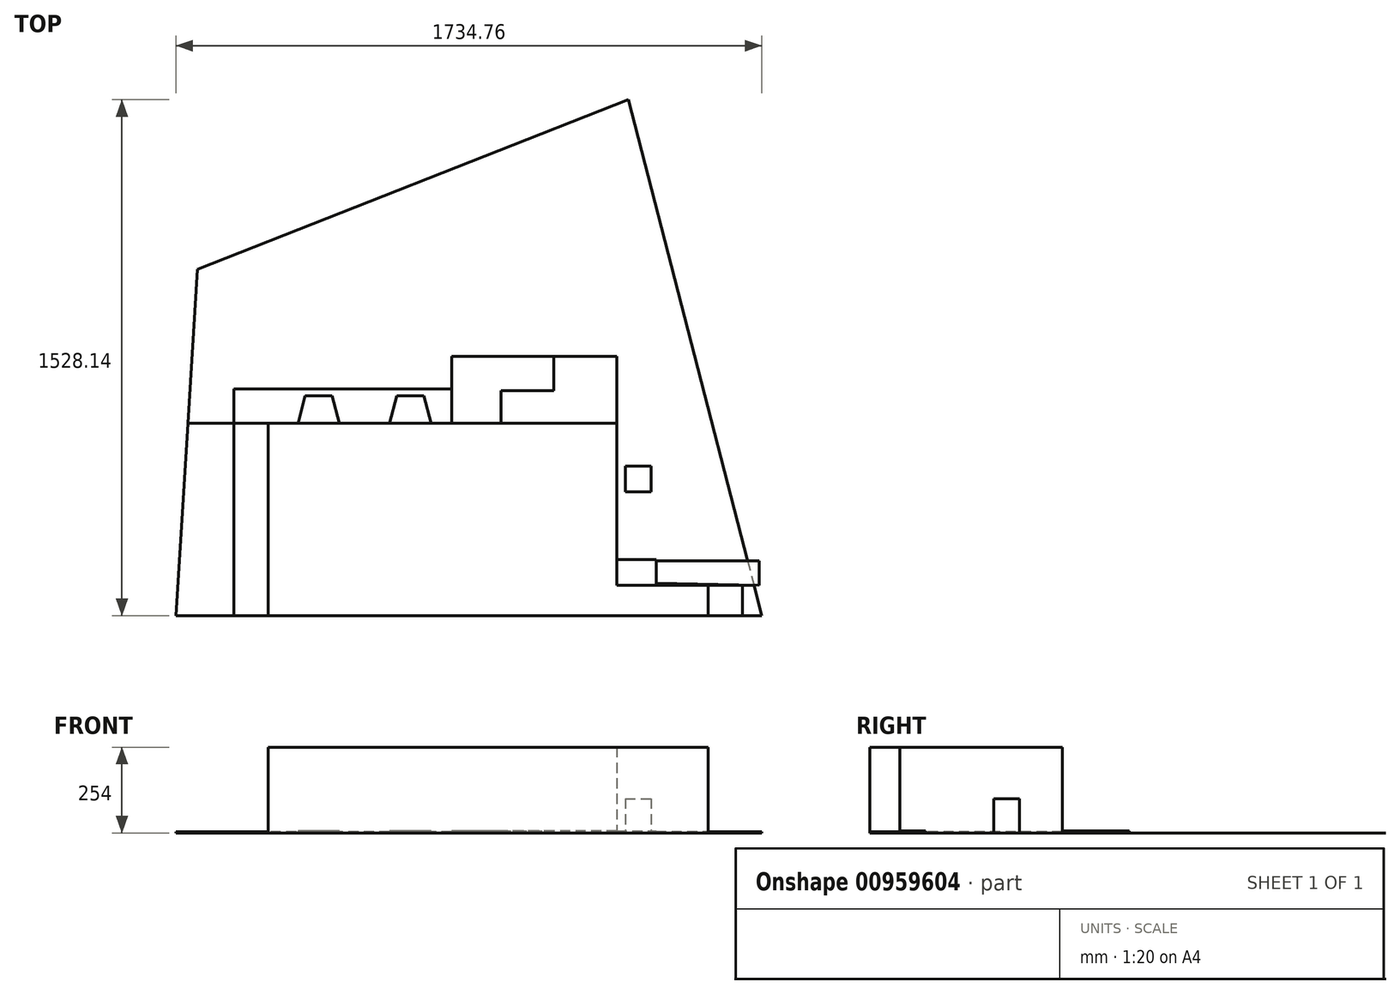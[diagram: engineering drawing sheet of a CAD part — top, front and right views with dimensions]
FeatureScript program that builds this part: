
annotation { "Feature Type Name" : "Feature", "Feature Type Description" : "" }
export const myFeature = defineFeature(function(context is Context, id is Id, definition is map)
    precondition{}
    {
        {
            var Q0;
            Q0=qCreatedBy(makeId("Top.planeOp"),FACE);
            var sketch = newSketch(context, id + "F0", { "sketchPlane" : qUnion([Q0])});
            skLineSegment(sketch, "E0", {"start": v(0, 0) * mm, "end": v(-1270, 0) * mm});
            skLineSegment(sketch, "E1", {"start": v(-1270, 0) * mm, "end": v(-1241.79, 456.33) * mm});
            skLineSegment(sketch, "E2", {"start": v(-1241.79, 456.33) * mm, "end": v(34.7, 958.18) * mm});
            skLineSegment(sketch, "E3", {"start": v(34.7, 958.18) * mm, "end": v(406.4, -480.48) * mm});
            skLineSegment(sketch, "E4", {"start": v(406.4, -480.48) * mm, "end": v(0, -480.48) * mm});
            skLineSegment(sketch, "E5", {"start": v(0, -480.48) * mm, "end": v(0, 0) * mm});
            skSolve(sketch);
        }
        {
            var Q0;
            Q0=makeQuery(id+"F0.imprint","IMPRINT",FACE,{"disambiguationData":[TD([[makeQuery(id+"F0.imprint","IMPRINT",EDGE,{"derivedFrom":sQuery(id+"F0.wireOp",EDGE,"E0")}),-1.0]])]});
            var sketch = newSketch(context, id + "F1", { "sketchPlane" : qUnion([Q0])});
            skLineSegment(sketch, "E6", {"start": v(-1032.93, 0) * mm, "end": v(0, 0) * mm});
            skLineSegment(sketch, "E7", {"start": v(0, 0) * mm, "end": v(0, -480.48) * mm});
            skLineSegment(sketch, "E8", {"start": v(0, -480.48) * mm, "end": v(270.93, -480.48) * mm});
            skLineSegment(sketch, "E9", {"start": v(270.93, -480.48) * mm, "end": v(270.93, -569.96) * mm});
            skLineSegment(sketch, "E10", {"start": v(270.93, -569.96) * mm, "end": v(-1032.93, -569.96) * mm});
            skLineSegment(sketch, "E11", {"start": v(-1032.93, -569.96) * mm, "end": v(-1032.93, 0) * mm});
            skSolve(sketch);
        }
        {
            var Q0;
            Q0 = qSketchRegion(id + "F1", true);
            extrude(context, id + "F2", {"entities" : qUnion([Q0]), "depth" : 254 * mm, "offsetDistance" : 25.4 * mm});
        }
        {
            var Q0;
            Q0=makeQuery(id+"F0.imprint","IMPRINT",FACE,{"disambiguationData":[TD([[makeQuery(id+"F0.imprint","IMPRINT",EDGE,{"derivedFrom":sQuery(id+"F0.wireOp",EDGE,"E0")}),-1.0]])]});
            var sketch = newSketch(context, id + "F3", { "sketchPlane" : qUnion([Q0])});
            skLineSegment(sketch, "E12.bottom", {"start": v(0, -480.48) * mm, "end": v(116.42, -480.48) * mm});
            skLineSegment(sketch, "E12.top", {"start": v(0, -404.28) * mm, "end": v(116.42, -404.28) * mm});
            skLineSegment(sketch, "E12.left", {"start": v(0, -480.48) * mm, "end": v(0, -404.28) * mm});
            skLineSegment(sketch, "E12.right", {"start": v(116.42, -480.48) * mm, "end": v(116.42, -404.28) * mm});
            skLineSegment(sketch, "E13", {"start": v(-488.95, 0) * mm, "end": v(-342.9, 0) * mm});
            skLineSegment(sketch, "E14", {"start": v(-342.9, 0) * mm, "end": v(-342.9, 96.88) * mm});
            skLineSegment(sketch, "E15", {"start": v(-342.9, 96.88) * mm, "end": v(-186.27, 96.88) * mm});
            skLineSegment(sketch, "E16", {"start": v(-186.27, 96.88) * mm, "end": v(-186.27, 198.48) * mm});
            skLineSegment(sketch, "E17", {"start": v(-186.27, 198.48) * mm, "end": v(-488.95, 198.48) * mm});
            skLineSegment(sketch, "E18", {"start": v(-488.95, 198.48) * mm, "end": v(-488.95, 0) * mm});
            skSolve(sketch);
        }
        {
            var Q0;
            Q0 = qSketchRegion(id + "F3", true);
            extrude(context, id + "F4", {"entities" : qUnion([Q0]), "depth" : 6.35 * mm, "offsetDistance" : 25.4 * mm});
        }
        {
            var Q0;
            Q0=makeQuery(id+"F0.imprint","IMPRINT",FACE,{"disambiguationData":[TD([[makeQuery(id+"F0.imprint","IMPRINT",EDGE,{"derivedFrom":sQuery(id+"F0.wireOp",EDGE,"E0")}),-1.0]])]});
            var sketch = newSketch(context, id + "F5", { "sketchPlane" : qUnion([Q0])});
            skLineSegment(sketch, "E19.bottom", {"start": v(25.4, -127) * mm, "end": v(101.6, -127) * mm});
            skLineSegment(sketch, "E19.top", {"start": v(25.4, -203.2) * mm, "end": v(101.6, -203.2) * mm});
            skLineSegment(sketch, "E19.left", {"start": v(25.4, -127) * mm, "end": v(25.4, -203.2) * mm});
            skLineSegment(sketch, "E19.right", {"start": v(101.6, -127) * mm, "end": v(101.6, -203.2) * mm});
            skSolve(sketch);
        }
        {
            var Q0;
            Q0 = qSketchRegion(id + "F5", true);
            extrude(context, id + "F6", {"entities" : qUnion([Q0]), "depth" : 101.6 * mm, "offsetDistance" : 25.4 * mm});
        }
        {
            var Q0;
            Q0=makeQuery(id+"F0.imprint","IMPRINT",FACE,{"disambiguationData":[TD([[makeQuery(id+"F0.imprint","IMPRINT",EDGE,{"derivedFrom":sQuery(id+"F0.wireOp",EDGE,"E0")}),-1.0]])]});
            var sketch = newSketch(context, id + "F7", { "sketchPlane" : qUnion([Q0])});
            skLineSegment(sketch, "E20", {"start": v(-550.33, 0) * mm, "end": v(-571.89, 80.43) * mm});
            skLineSegment(sketch, "E21", {"start": v(-571.89, 80.43) * mm, "end": v(-651.55, 80.43) * mm});
            skLineSegment(sketch, "E22", {"start": v(-651.55, 80.43) * mm, "end": v(-673.1, 0) * mm});
            skLineSegment(sketch, "E23", {"start": v(-673.1, 0) * mm, "end": v(-550.33, 0) * mm});
            skLineSegment(sketch, "E24", {"start": v(-821.27, 0) * mm, "end": v(-842.82, 80.43) * mm});
            skLineSegment(sketch, "E25", {"start": v(-842.82, 80.43) * mm, "end": v(-922.48, 80.43) * mm});
            skLineSegment(sketch, "E26", {"start": v(-922.48, 80.43) * mm, "end": v(-944.03, 0) * mm});
            skLineSegment(sketch, "E27", {"start": v(-944.03, 0) * mm, "end": v(-821.27, 0) * mm});
            skSolve(sketch);
        }
        {
            var Q0;
            Q0 = qSketchRegion(id + "F7", true);
            extrude(context, id + "F8", {"entities" : qUnion([Q0]), "depth" : 6.35 * mm, "offsetDistance" : 25.4 * mm});
        }
        {
            var Q0;
            Q0=makeQuery(id+"F0.imprint","IMPRINT",FACE,{"disambiguationData":[TD([[makeQuery(id+"F0.imprint","IMPRINT",EDGE,{"derivedFrom":sQuery(id+"F0.wireOp",EDGE,"E0")}),-1.0]])]});
            var sketch = newSketch(context, id + "F9", { "sketchPlane" : qUnion([Q0])});
            skLineSegment(sketch, "E28.bottom", {"start": v(-1032.93, 0) * mm, "end": v(-1134.53, 0) * mm});
            skLineSegment(sketch, "E28.top", {"start": v(-1032.93, -569.96) * mm, "end": v(-1134.53, -569.96) * mm});
            skLineSegment(sketch, "E28.left", {"start": v(-1032.93, 0) * mm, "end": v(-1032.93, -569.96) * mm});
            skLineSegment(sketch, "E28.right", {"start": v(-1134.53, 0) * mm, "end": v(-1134.53, -569.96) * mm});
            skLineSegment(sketch, "E29.bottom", {"start": v(270.93, -480.48) * mm, "end": v(372.53, -480.48) * mm});
            skLineSegment(sketch, "E29.top", {"start": v(270.93, -569.96) * mm, "end": v(372.53, -569.96) * mm});
            skLineSegment(sketch, "E29.left", {"start": v(270.93, -480.48) * mm, "end": v(270.93, -569.96) * mm});
            skLineSegment(sketch, "E29.right", {"start": v(372.53, -480.48) * mm, "end": v(372.53, -569.96) * mm});
            skSolve(sketch);
        }
        {
            var Q0;
            Q0 = qSketchRegion(id + "F9", true);
            extrude(context, id + "F10", {"entities" : qUnion([Q0]), "depth" : 3.8 * mm, "offsetDistance" : 25.4 * mm});
        }
        {
            var Q0;
            Q0=makeQuery(id+"F0.imprint","IMPRINT",FACE,{"disambiguationData":[TD([[makeQuery(id+"F0.imprint","IMPRINT",EDGE,{"derivedFrom":sQuery(id+"F0.wireOp",EDGE,"E0")}),-1.0]])]});
            var sketch = newSketch(context, id + "F11", { "sketchPlane" : qUnion([Q0])});
            skLineSegment(sketch, "E30", {"start": v(406.4, -480.48) * mm, "end": v(429.52, -569.96) * mm});
            skLineSegment(sketch, "E31", {"start": v(429.52, -569.96) * mm, "end": v(372.53, -569.96) * mm});
            skLineSegment(sketch, "E32", {"start": v(372.53, -569.96) * mm, "end": v(372.53, -480.48) * mm});
            skLineSegment(sketch, "E33", {"start": v(372.53, -480.48) * mm, "end": v(406.4, -480.48) * mm});
            skLineSegment(sketch, "E34", {"start": v(-1134.53, 0) * mm, "end": v(-1270, 0) * mm});
            skLineSegment(sketch, "E35", {"start": v(-1270, 0) * mm, "end": v(-1305.24, -569.96) * mm});
            skLineSegment(sketch, "E36", {"start": v(-1305.24, -569.96) * mm, "end": v(-1134.53, -569.96) * mm});
            skLineSegment(sketch, "E37", {"start": v(-1134.53, -569.96) * mm, "end": v(-1134.53, 0) * mm});
            skSolve(sketch);
        }
        {
            var Q0;
            Q0 = qSketchRegion(id + "F11", true);
            var Q1;
            Q1=makeQuery(id+"F10.opExtrude","CAP_FACE",FACE,{"disambiguationData":[OSD([sQuery(id+"F9.wireOp",EDGE,"E28.bottom"),sQuery(id+"F9.wireOp",EDGE,"E28.top"),sQuery(id+"F9.wireOp",EDGE,"E28.left"),sQuery(id+"F9.wireOp",EDGE,"E28.right")])],"isStart":false});
            extrude(context, id + "F12", {"entities" : qUnion([Q0]), "endBound" : BoundingType.UP_TO_SURFACE, "depth" : 25.4 * mm, "endBoundEntityFace" : qUnion([Q1]), "offsetDistance" : 25.4 * mm});
        }
        {
            var Q0;
            Q0=makeQuery(id+"F0.imprint","IMPRINT",FACE,{"disambiguationData":[TD([[makeQuery(id+"F0.imprint","IMPRINT",EDGE,{"derivedFrom":sQuery(id+"F0.wireOp",EDGE,"E0")}),-1.0]])]});
            var sketch = newSketch(context, id + "F13", { "sketchPlane" : qUnion([Q0])});
            skLineSegment(sketch, "E38.bottom", {"start": v(-488.95, 0) * mm, "end": v(-1134.53, 0) * mm});
            skLineSegment(sketch, "E38.top", {"start": v(-488.95, 101.6) * mm, "end": v(-1134.53, 101.6) * mm});
            skLineSegment(sketch, "E38.left", {"start": v(-488.95, 0) * mm, "end": v(-488.95, 101.6) * mm});
            skLineSegment(sketch, "E38.right", {"start": v(-1134.53, 0) * mm, "end": v(-1134.53, 101.6) * mm});
            skLineSegment(sketch, "E39", {"start": v(422.34, -480.52) * mm, "end": v(422.34, -407.47) * mm});
            skLineSegment(sketch, "E40", {"start": v(422.34, -407.47) * mm, "end": v(117.59, -407.47) * mm});
            skLineSegment(sketch, "E41", {"start": v(117.59, -407.47) * mm, "end": v(117.59, -474.26) * mm});
            skLineSegment(sketch, "E42", {"start": v(117.59, -474.26) * mm, "end": v(422.34, -480.52) * mm});
            skSolve(sketch);
        }
        {
            var Q0;
            Q0 = qSketchRegion(id + "F13", true);
            var Q1;
            Q1=makeQuery(id+"F10.opExtrude","CAP_FACE",FACE,{"disambiguationData":[OSD([sQuery(id+"F9.wireOp",EDGE,"E28.bottom"),sQuery(id+"F9.wireOp",EDGE,"E28.top"),sQuery(id+"F9.wireOp",EDGE,"E28.left"),sQuery(id+"F9.wireOp",EDGE,"E28.right")])],"isStart":false});
            extrude(context, id + "F14", {"entities" : qUnion([Q0]), "endBound" : BoundingType.UP_TO_SURFACE, "depth" : 25.4 * mm, "endBoundEntityFace" : qUnion([Q1]), "offsetDistance" : 25.4 * mm});
        }
        {
            var Q0;
            Q0=makeQuery(id+"F0.imprint","IMPRINT",FACE,{"disambiguationData":[TD([[makeQuery(id+"F0.imprint","IMPRINT",EDGE,{"derivedFrom":sQuery(id+"F0.wireOp",EDGE,"E0")}),-1.0]])]});
            var sketch = newSketch(context, id + "F15", { "sketchPlane" : qUnion([Q0])});
            skLineSegment(sketch, "E43", {"start": v(-186.27, 198.48) * mm, "end": v(-186.27, 96.88) * mm});
            skLineSegment(sketch, "E44", {"start": v(-186.27, 96.88) * mm, "end": v(-342.9, 96.88) * mm});
            skLineSegment(sketch, "E45", {"start": v(-342.9, 96.88) * mm, "end": v(-342.9, 0) * mm});
            skLineSegment(sketch, "E46", {"start": v(-342.9, 0) * mm, "end": v(0, 0) * mm});
            skLineSegment(sketch, "E47", {"start": v(0, 0) * mm, "end": v(0, 198.48) * mm});
            skLineSegment(sketch, "E48", {"start": v(0, 198.48) * mm, "end": v(-186.27, 198.48) * mm});
            skSolve(sketch);
        }
        {
            var Q0;
            Q0 = qSketchRegion(id + "F15", true);
            var Q1;
            Q1=makeQuery(id+"F4.opExtrude","CAP_FACE",FACE,{"disambiguationData":[OSD([sQuery(id+"F3.wireOp",EDGE,"E13"),sQuery(id+"F3.wireOp",EDGE,"E14"),sQuery(id+"F3.wireOp",EDGE,"E15"),sQuery(id+"F3.wireOp",EDGE,"E16"),sQuery(id+"F3.wireOp",EDGE,"E17"),sQuery(id+"F3.wireOp",EDGE,"E18")])],"isStart":false});
            extrude(context, id + "F16", {"entities" : qUnion([Q0]), "endBound" : BoundingType.UP_TO_SURFACE, "depth" : 25.4 * mm, "endBoundEntityFace" : qUnion([Q1]), "offsetDistance" : 25.4 * mm});
        }
        {
            var Q0;
            Q0 = qSketchRegion(id + "F0", true);
            extrude(context, id + "F17", {"entities" : qUnion([Q0]), "depth" : 0.25 * mm, "offsetDistance" : 25.4 * mm});
        }
    });
